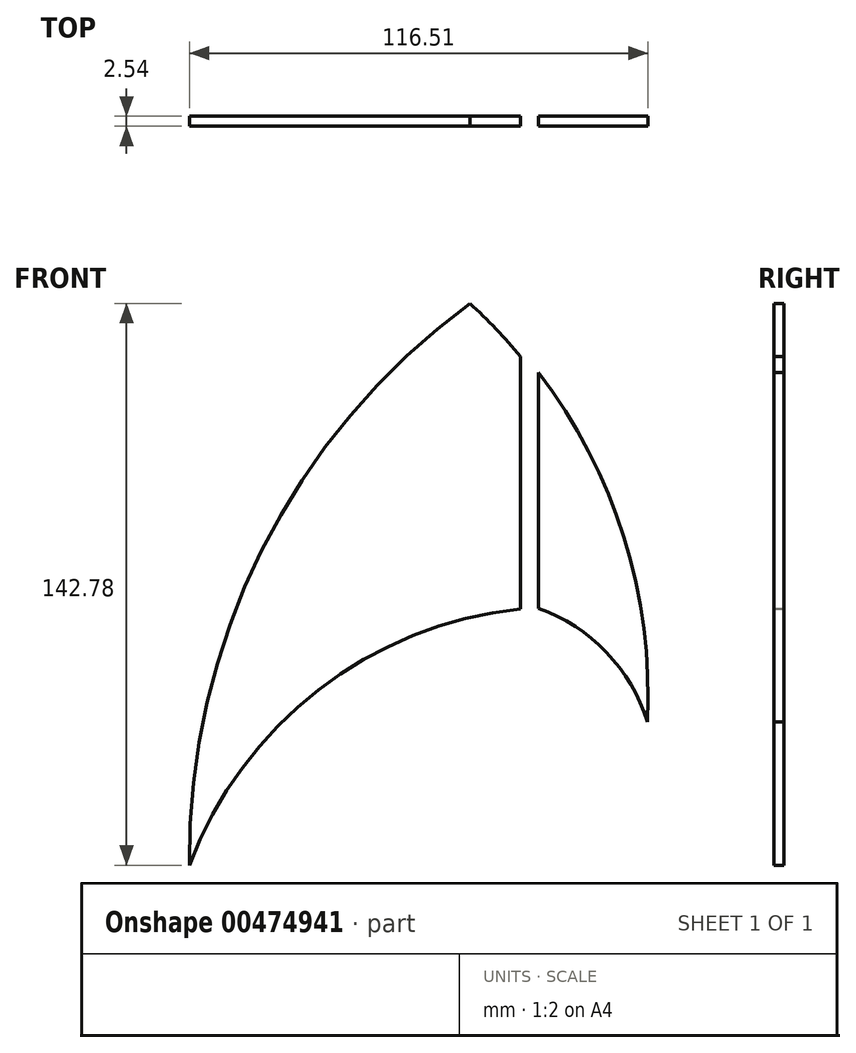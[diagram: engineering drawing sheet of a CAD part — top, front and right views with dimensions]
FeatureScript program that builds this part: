
annotation { "Feature Type Name" : "Feature", "Feature Type Description" : "" }
export const myFeature = defineFeature(function(context is Context, id is Id, definition is map)
    precondition{}
    {
        {
            var Q0;
            Q0=qCreatedBy(makeId("Front.planeOp"),FACE);
            var sketch = newSketch(context, id + "F0", { "sketchPlane" : qUnion([Q0])});
            skArc(sketch, "E0", {"start": v(-28.44, 114.38) * mm, "mid": v(-81.3, 51.6) * mm, "end": v(-99.67, -28.4) * mm});
            skArc(sketch, "E1", {"start": v(-15.57, 36.77) * mm, "mid": v(-66.9, 16.16) * mm, "end": v(-99.67, -28.4) * mm});
            skLineSegment(sketch, "E2", {"start": v(-15.57, 36.77) * mm, "end": v(-15.57, 100.83) * mm});
            skArc(sketch, "E3.trimOffspring", {"start": v(-15.57, 100.83) * mm, "mid": v(-21.77, 107.83) * mm, "end": v(-28.44, 114.38) * mm});
            skArc(sketch, "E4", {"start": v(16.66, 8.02) * mm, "mid": v(10.72, 54.85) * mm, "end": v(-11, 96.75) * mm});
            skArc(sketch, "E5", {"start": v(16.66, 8.02) * mm, "mid": v(6.25, 25.74) * mm, "end": v(-11, 36.9) * mm});
            skLineSegment(sketch, "E6", {"start": v(-11, 96.75) * mm, "end": v(-11, 36.9) * mm});
            skSolve(sketch);
        }
        {
            var Q0;
            Q0=makeQuery(id+"F0.imprint","IMPRINT",FACE,{"disambiguationData":[TD([[makeQuery(id+"F0.imprint","IMPRINT",EDGE,{"derivedFrom":sQuery(id+"F0.wireOp",EDGE,"E0")}),1.0]])]});
            var Q1;
            Q1=makeQuery(id+"F0.imprint","IMPRINT",FACE,{"disambiguationData":[TD([[makeQuery(id+"F0.imprint","IMPRINT",EDGE,{"derivedFrom":sQuery(id+"F0.wireOp",EDGE,"E4")}),1.0]])]});
            extrude(context, id + "F1", {"entities" : qUnion([Q0, Q1]), "depth" : 2.54 * mm});
        }
    });
